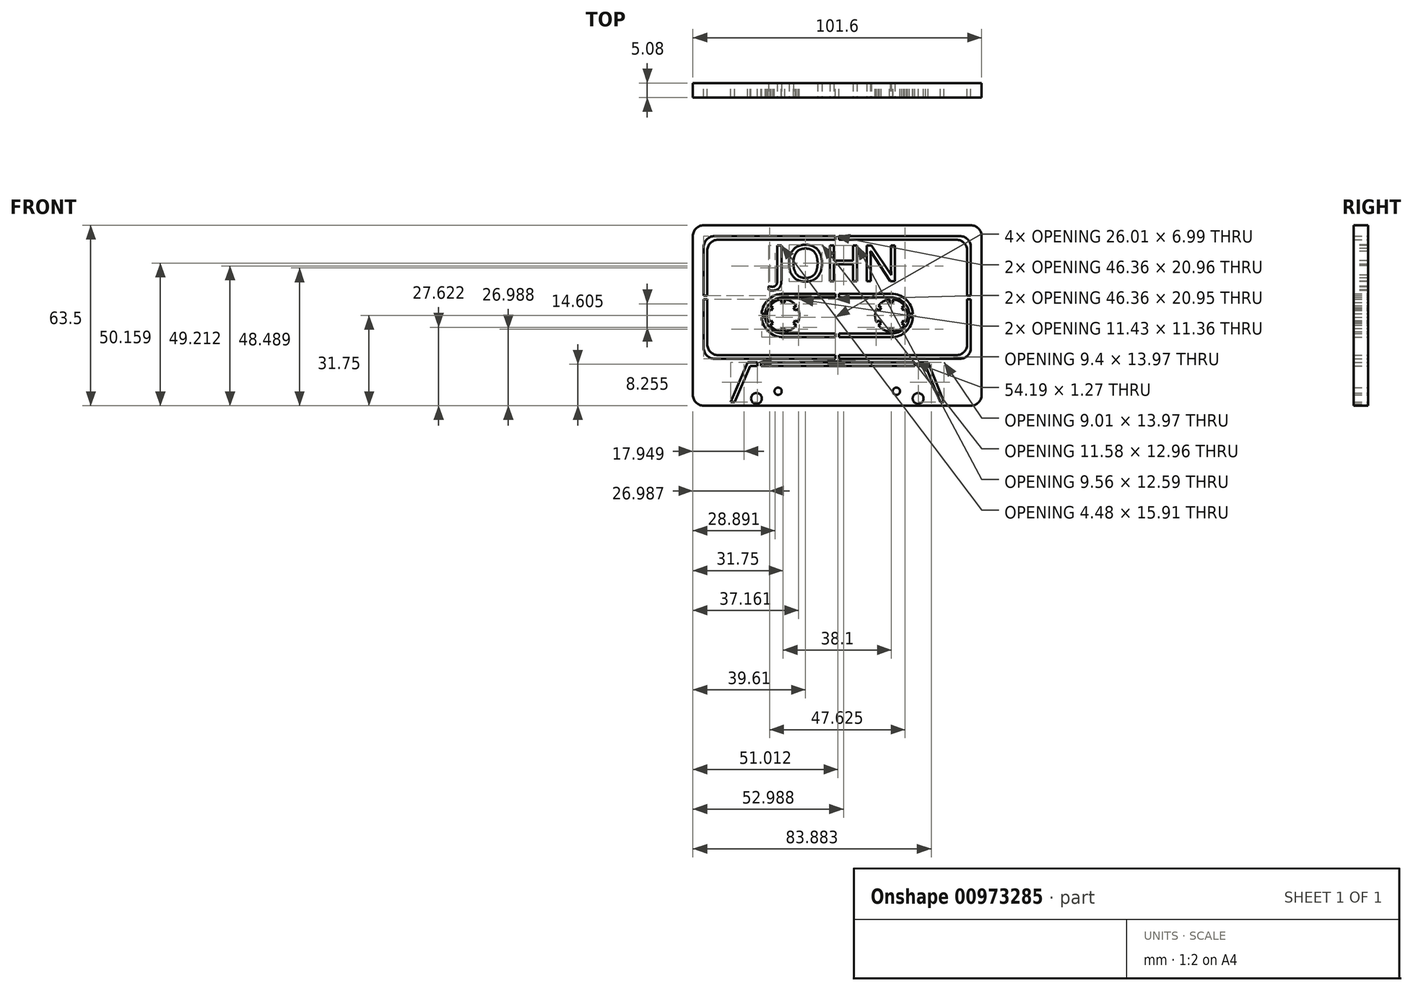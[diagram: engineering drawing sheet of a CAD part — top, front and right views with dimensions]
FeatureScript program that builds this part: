
annotation { "Feature Type Name" : "Feature", "Feature Type Description" : "" }
export const myFeature = defineFeature(function(context is Context, id is Id, definition is map)
    precondition{}
    {
        {
            var Q0;
            Q0=qCreatedBy(makeId("Front.planeOp"),FACE);
            var sketch = newSketch(context, id + "F0", { "sketchPlane" : qUnion([Q0])});
            skLineSegment(sketch, "E0.bottom", {"start": v(47, 31.75) * mm, "end": v(-47, 31.75) * mm});
            skLineSegment(sketch, "E0.top", {"start": v(47, -31.75) * mm, "end": v(-47, -31.75) * mm});
            skLineSegment(sketch, "E0.left", {"start": v(50.8, 27.94) * mm, "end": v(50.8, -27.94) * mm});
            skLineSegment(sketch, "E0.right", {"start": v(-50.8, 27.94) * mm, "end": v(-50.8, -27.94) * mm});
            skPoint(sketch, "E0.middle", {"position": v(0, 0) * mm});
            skPoint(sketch, "E1.visualSharp", {"position": v(50.8, 31.75) * mm});
            skArc(sketch, "E1.filletArc", {"start": v(50.8, 27.94) * mm, "mid": v(49.68, 30.63) * mm, "end": v(47, 31.75) * mm});
            skPoint(sketch, "E2.visualSharp", {"position": v(-50.8, 31.75) * mm});
            skArc(sketch, "E2.filletArc", {"start": v(-47, 31.75) * mm, "mid": v(-49.68, 30.63) * mm, "end": v(-50.8, 27.94) * mm});
            skPoint(sketch, "E3.visualSharp", {"position": v(-50.8, -31.75) * mm});
            skArc(sketch, "E3.filletArc", {"start": v(-50.8, -27.94) * mm, "mid": v(-49.68, -30.63) * mm, "end": v(-47, -31.75) * mm});
            skPoint(sketch, "E4.visualSharp", {"position": v(50.8, -31.75) * mm});
            skArc(sketch, "E4.filletArc", {"start": v(47, -31.75) * mm, "mid": v(49.68, -30.63) * mm, "end": v(50.8, -27.94) * mm});
            skLineSegment(sketch, "E5.bottom", {"start": v(-43.18, 27.94) * mm, "end": v(-0.64, 27.94) * mm});
            skLineSegment(sketch, "E5.top", {"start": v(-43.18, -15.24) * mm, "end": v(-0.64, -15.24) * mm});
            skLineSegment(sketch, "E5.left", {"start": v(-47, 24.13) * mm, "end": v(-47, 6.98) * mm});
            skLineSegment(sketch, "E5.right", {"start": v(47, 24.13) * mm, "end": v(47, 6.99) * mm});
            skLineSegment(sketch, "E6.bottom", {"start": v(-41.91, 26.67) * mm, "end": v(-0.63, 26.67) * mm});
            skLineSegment(sketch, "E6.top", {"start": v(-41.91, -13.97) * mm, "end": v(-0.63, -13.97) * mm});
            skLineSegment(sketch, "E6.left", {"start": v(-45.72, 22.86) * mm, "end": v(-45.72, 6.98) * mm});
            skLineSegment(sketch, "E6.right", {"start": v(45.72, 22.86) * mm, "end": v(45.72, 6.99) * mm});
            skArc(sketch, "E7.filletArc", {"start": v(47, 24.13) * mm, "mid": v(45.87, 26.82) * mm, "end": v(43.18, 27.94) * mm});
            skPoint(sketch, "E8.visualSharp", {"position": v(45.72, 26.67) * mm});
            skArc(sketch, "E8.filletArc", {"start": v(45.72, 22.86) * mm, "mid": v(44.6, 25.55) * mm, "end": v(41.91, 26.67) * mm});
            skPoint(sketch, "E9.visualSharp", {"position": v(47, -15.24) * mm});
            skArc(sketch, "E9.filletArc", {"start": v(43.18, -15.24) * mm, "mid": v(45.87, -14.12) * mm, "end": v(47, -11.43) * mm});
            skPoint(sketch, "E10.visualSharp", {"position": v(45.72, -13.97) * mm});
            skArc(sketch, "E10.filletArc", {"start": v(41.91, -13.97) * mm, "mid": v(44.6, -12.85) * mm, "end": v(45.72, -10.16) * mm});
            skPoint(sketch, "E11.visualSharp", {"position": v(-47, -15.24) * mm});
            skArc(sketch, "E11.filletArc", {"start": v(-47, -11.43) * mm, "mid": v(-45.87, -14.12) * mm, "end": v(-43.18, -15.24) * mm});
            skPoint(sketch, "E12.visualSharp", {"position": v(-45.72, -13.97) * mm});
            skArc(sketch, "E12.filletArc", {"start": v(-45.72, -10.16) * mm, "mid": v(-44.6, -12.85) * mm, "end": v(-41.91, -13.97) * mm});
            skArc(sketch, "E13.filletArc", {"start": v(-43.18, 27.94) * mm, "mid": v(-45.87, 26.82) * mm, "end": v(-47, 24.13) * mm});
            skPoint(sketch, "E14.visualSharp", {"position": v(-45.72, 26.67) * mm});
            skArc(sketch, "E14.filletArc", {"start": v(-41.91, 26.67) * mm, "mid": v(-44.6, 25.55) * mm, "end": v(-45.72, 22.86) * mm});
            skLineSegment(sketch, "E15", {"start": v(0.64, -15.24) * mm, "end": v(0.64, -13.97) * mm});
            skLineSegment(sketch, "E16", {"start": v(-0.64, -15.24) * mm, "end": v(-0.64, -13.97) * mm});
            skLineSegment(sketch, "E17.trimOffspring", {"start": v(-0.64, 26.67) * mm, "end": v(-0.64, 27.94) * mm});
            skLineSegment(sketch, "E18.trimOffspring", {"start": v(0.64, 26.67) * mm, "end": v(0.64, 27.94) * mm});
            skLineSegment(sketch, "E19.trimOffspring", {"start": v(0.63, -13.97) * mm, "end": v(41.91, -13.97) * mm});
            skLineSegment(sketch, "E20.trimOffspring", {"start": v(0.64, -15.24) * mm, "end": v(43.18, -15.24) * mm});
            skLineSegment(sketch, "E21.trimOffspring", {"start": v(0.64, 27.94) * mm, "end": v(43.18, 27.94) * mm});
            skLineSegment(sketch, "E22.trimOffspring", {"start": v(0.63, 26.67) * mm, "end": v(41.91, 26.67) * mm});
            skLineSegment(sketch, "E23", {"start": v(-47, 6.98) * mm, "end": v(-45.72, 6.99) * mm});
            skLineSegment(sketch, "E24", {"start": v(-47, 5.71) * mm, "end": v(-45.72, 5.71) * mm});
            skLineSegment(sketch, "E25.trimOffspring", {"start": v(45.72, 6.99) * mm, "end": v(47, 6.99) * mm});
            skLineSegment(sketch, "E26.trimOffspring", {"start": v(45.72, 5.72) * mm, "end": v(47, 5.72) * mm});
            skPoint(sketch, "E27.orphan", {"position": v(48.52, 5.72) * mm});
            skPoint(sketch, "E28.orphan", {"position": v(48.52, 6.99) * mm});
            skLineSegment(sketch, "E29.trimOffspring", {"start": v(47, 5.72) * mm, "end": v(47, -11.43) * mm});
            skLineSegment(sketch, "E30.trimOffspring", {"start": v(45.72, 5.72) * mm, "end": v(45.72, -10.16) * mm});
            skLineSegment(sketch, "E31.trimOffspring", {"start": v(-45.72, 5.71) * mm, "end": v(-45.72, -10.16) * mm});
            skLineSegment(sketch, "E32.trimOffspring", {"start": v(-47, 5.71) * mm, "end": v(-47, -11.43) * mm});
            skLineSegment(sketch, "E33.bottom", {"start": v(-19.05, 6.35) * mm, "end": v(-0.63, 6.35) * mm});
            skLineSegment(sketch, "E33.top", {"start": v(-19.05, -6.35) * mm, "end": v(-0.63, -6.35) * mm});
            skLineSegment(sketch, "E34.bottom", {"start": v(-19.05, 7.62) * mm, "end": v(-0.63, 7.62) * mm});
            skLineSegment(sketch, "E34.top", {"start": v(-19.05, -7.62) * mm, "end": v(-0.63, -7.62) * mm});
            skLineSegment(sketch, "E35", {"start": v(-0.63, 7.62) * mm, "end": v(-0.63, 6.35) * mm});
            skLineSegment(sketch, "E36", {"start": v(0.63, 7.62) * mm, "end": v(0.63, 6.35) * mm});
            skLineSegment(sketch, "E37.trimOffspring", {"start": v(-0.63, -6.35) * mm, "end": v(-0.63, -7.62) * mm});
            skLineSegment(sketch, "E38.trimOffspring", {"start": v(0.63, -6.35) * mm, "end": v(0.63, -7.62) * mm});
            skLineSegment(sketch, "E39.trimOffspring", {"start": v(0.64, -7.62) * mm, "end": v(19.05, -7.62) * mm});
            skLineSegment(sketch, "E40.trimOffspring", {"start": v(0.63, -6.35) * mm, "end": v(19.05, -6.35) * mm});
            skLineSegment(sketch, "E41.trimOffspring", {"start": v(0.63, 7.62) * mm, "end": v(19.05, 7.62) * mm});
            skLineSegment(sketch, "E42.trimOffspring", {"start": v(0.64, 6.35) * mm, "end": v(23.26, 6.35) * mm});
            skArc(sketch, "E43", {"start": v(-19.69, 5.68) * mm, "mid": v(-21.9, 4.95) * mm, "end": v(-23.65, 3.39) * mm});
            skArc(sketch, "E44", {"start": v(18.41, 5.68) * mm, "mid": v(16.2, 4.95) * mm, "end": v(14.45, 3.39) * mm});
            skArc(sketch, "E45", {"start": v(-19.05, 7.62) * mm, "mid": v(-24.2, 5.6) * mm, "end": v(-26.64, 0.64) * mm});
            skArc(sketch, "E46", {"start": v(-19.05, 6.35) * mm, "mid": v(-23.3, 4.7) * mm, "end": v(-25.37, 0.63) * mm});
            skArc(sketch, "E47", {"start": v(19.05, 7.62) * mm, "mid": v(24.2, 5.6) * mm, "end": v(26.64, 0.64) * mm});
            skArc(sketch, "E48", {"start": v(19.05, 6.35) * mm, "mid": v(23.3, 4.7) * mm, "end": v(25.37, 0.63) * mm});
            skLineSegment(sketch, "E49", {"start": v(-26.64, 0.64) * mm, "end": v(-25.37, 0.64) * mm});
            skLineSegment(sketch, "E50", {"start": v(-26.64, -0.64) * mm, "end": v(-25.37, -0.64) * mm});
            skArc(sketch, "E51.trimOffspring", {"start": v(-26.64, -0.64) * mm, "mid": v(-24.2, -5.6) * mm, "end": v(-19.05, -7.62) * mm});
            skArc(sketch, "E52.trimOffspring", {"start": v(-25.37, -0.64) * mm, "mid": v(-23.3, -4.7) * mm, "end": v(-19.05, -6.35) * mm});
            skLineSegment(sketch, "E53.trimOffspring", {"start": v(25.37, 0.64) * mm, "end": v(26.64, 0.64) * mm});
            skLineSegment(sketch, "E54.trimOffspring", {"start": v(25.37, -0.64) * mm, "end": v(26.64, -0.64) * mm});
            skArc(sketch, "E55.trimOffspring", {"start": v(25.37, -0.64) * mm, "mid": v(23.3, -4.7) * mm, "end": v(19.05, -6.35) * mm});
            skArc(sketch, "E56.trimOffspring", {"start": v(26.64, -0.64) * mm, "mid": v(24.2, -5.6) * mm, "end": v(19.05, -7.62) * mm});
            skLineSegment(sketch, "E57", {"start": v(-18.41, 5.68) * mm, "end": v(-18.41, 4.57) * mm});
            skLineSegment(sketch, "E58", {"start": v(-18.41, 4.57) * mm, "end": v(-19.69, 4.57) * mm});
            skLineSegment(sketch, "E59", {"start": v(-19.69, 4.57) * mm, "end": v(-19.69, 5.68) * mm});
            skLineSegment(sketch, "E60.MirrorCS", {"start": v(18.41, 5.68) * mm, "end": v(18.41, 4.57) * mm});
            skLineSegment(sketch, "E61.MirrorCS", {"start": v(18.41, 4.57) * mm, "end": v(19.69, 4.57) * mm});
            skLineSegment(sketch, "E62.MirrorCS", {"start": v(19.69, 4.57) * mm, "end": v(19.69, 5.68) * mm});
            skLineSegment(sketch, "E63.1.0", {"start": v(-23.65, 3.39) * mm, "end": v(-22.7, 2.84) * mm});
            skLineSegment(sketch, "E63.1.1", {"start": v(-22.7, 2.84) * mm, "end": v(-23.33, 1.74) * mm});
            skLineSegment(sketch, "E63.1.2", {"start": v(-23.33, 1.74) * mm, "end": v(-24.29, 2.29) * mm});
            skLineSegment(sketch, "E63.2.0", {"start": v(-24.29, -2.29) * mm, "end": v(-23.33, -1.74) * mm});
            skLineSegment(sketch, "E63.2.1", {"start": v(-23.33, -1.74) * mm, "end": v(-22.7, -2.84) * mm});
            skLineSegment(sketch, "E63.2.2", {"start": v(-22.7, -2.84) * mm, "end": v(-23.65, -3.39) * mm});
            skLineSegment(sketch, "E63.3.0", {"start": v(-19.69, -5.68) * mm, "end": v(-19.69, -4.57) * mm});
            skLineSegment(sketch, "E63.3.1", {"start": v(-19.69, -4.57) * mm, "end": v(-18.41, -4.57) * mm});
            skLineSegment(sketch, "E63.3.2", {"start": v(-18.41, -4.57) * mm, "end": v(-18.41, -5.68) * mm});
            skLineSegment(sketch, "E63.4.0", {"start": v(-14.45, -3.39) * mm, "end": v(-15.4, -2.84) * mm});
            skLineSegment(sketch, "E63.4.1", {"start": v(-15.4, -2.84) * mm, "end": v(-14.77, -1.74) * mm});
            skLineSegment(sketch, "E63.4.2", {"start": v(-14.77, -1.74) * mm, "end": v(-13.81, -2.29) * mm});
            skLineSegment(sketch, "E63.5.0", {"start": v(-13.81, 2.29) * mm, "end": v(-14.77, 1.74) * mm});
            skLineSegment(sketch, "E63.5.1", {"start": v(-14.77, 1.74) * mm, "end": v(-15.4, 2.84) * mm});
            skLineSegment(sketch, "E63.5.2", {"start": v(-15.4, 2.84) * mm, "end": v(-14.45, 3.39) * mm});
            skArc(sketch, "E64.trimOffspring", {"start": v(-14.45, 3.39) * mm, "mid": v(-16.2, 4.95) * mm, "end": v(-18.41, 5.68) * mm});
            skArc(sketch, "E65.trimOffspring", {"start": v(-13.81, -2.29) * mm, "mid": v(-13.33, 0) * mm, "end": v(-13.81, 2.29) * mm});
            skArc(sketch, "E66.trimOffspring", {"start": v(-18.41, -5.68) * mm, "mid": v(-16.2, -4.95) * mm, "end": v(-14.45, -3.39) * mm});
            skArc(sketch, "E67.trimOffspring", {"start": v(-23.65, -3.39) * mm, "mid": v(-21.9, -4.95) * mm, "end": v(-19.69, -5.68) * mm});
            skArc(sketch, "E68.trimOffspring", {"start": v(-24.29, 2.29) * mm, "mid": v(-24.77, 0) * mm, "end": v(-24.29, -2.29) * mm});
            skLineSegment(sketch, "E69.1.0", {"start": v(15.4, 2.84) * mm, "end": v(14.45, 3.39) * mm});
            skLineSegment(sketch, "E69.1.1", {"start": v(14.77, 1.74) * mm, "end": v(15.4, 2.84) * mm});
            skLineSegment(sketch, "E69.1.2", {"start": v(13.81, 2.29) * mm, "end": v(14.77, 1.74) * mm});
            skLineSegment(sketch, "E69.2.0", {"start": v(14.77, -1.74) * mm, "end": v(13.81, -2.29) * mm});
            skLineSegment(sketch, "E69.2.1", {"start": v(15.4, -2.84) * mm, "end": v(14.77, -1.74) * mm});
            skLineSegment(sketch, "E69.2.2", {"start": v(14.45, -3.39) * mm, "end": v(15.4, -2.84) * mm});
            skLineSegment(sketch, "E69.3.0", {"start": v(18.41, -4.57) * mm, "end": v(18.41, -5.68) * mm});
            skLineSegment(sketch, "E69.3.1", {"start": v(19.69, -4.57) * mm, "end": v(18.41, -4.57) * mm});
            skLineSegment(sketch, "E69.3.2", {"start": v(19.69, -5.68) * mm, "end": v(19.69, -4.57) * mm});
            skLineSegment(sketch, "E69.4.0", {"start": v(22.7, -2.84) * mm, "end": v(23.65, -3.39) * mm});
            skLineSegment(sketch, "E69.4.1", {"start": v(23.33, -1.74) * mm, "end": v(22.7, -2.84) * mm});
            skLineSegment(sketch, "E69.4.2", {"start": v(24.29, -2.29) * mm, "end": v(23.33, -1.74) * mm});
            skLineSegment(sketch, "E69.5.0", {"start": v(23.33, 1.74) * mm, "end": v(24.29, 2.29) * mm});
            skLineSegment(sketch, "E69.5.1", {"start": v(22.7, 2.84) * mm, "end": v(23.33, 1.74) * mm});
            skLineSegment(sketch, "E69.5.2", {"start": v(23.65, 3.39) * mm, "end": v(22.7, 2.84) * mm});
            skArc(sketch, "E70.trimOffspring", {"start": v(23.65, 3.39) * mm, "mid": v(21.9, 4.95) * mm, "end": v(19.69, 5.68) * mm});
            skArc(sketch, "E71.trimOffspring", {"start": v(24.29, -2.29) * mm, "mid": v(24.77, 0) * mm, "end": v(24.29, 2.29) * mm});
            skArc(sketch, "E72.trimOffspring", {"start": v(19.69, -5.68) * mm, "mid": v(21.9, -4.95) * mm, "end": v(23.65, -3.39) * mm});
            skArc(sketch, "E73.trimOffspring", {"start": v(14.45, -3.39) * mm, "mid": v(16.2, -4.95) * mm, "end": v(18.41, -5.68) * mm});
            skArc(sketch, "E74.trimOffspring", {"start": v(13.81, 2.29) * mm, "mid": v(13.33, 0) * mm, "end": v(13.81, -2.29) * mm});
            skLineSegment(sketch, "E75", {"start": v(-37.55, -30.48) * mm, "end": v(-31.53, -16.51) * mm});
            skLineSegment(sketch, "E76", {"start": v(-31.53, -16.51) * mm, "end": v(-28.15, -16.51) * mm});
            skLineSegment(sketch, "E77", {"start": v(31.97, -16.5) * mm, "end": v(37.59, -30.48) * mm});
            skLineSegment(sketch, "E78", {"start": v(-36.17, -30.48) * mm, "end": v(-30.7, -17.78) * mm});
            skLineSegment(sketch, "E79", {"start": v(-30.7, -17.78) * mm, "end": v(-28.15, -17.78) * mm});
            skLineSegment(sketch, "E80", {"start": v(31.12, -17.78) * mm, "end": v(36.22, -30.48) * mm});
            skLineSegment(sketch, "E81", {"start": v(-37.55, -30.48) * mm, "end": v(-36.17, -30.48) * mm});
            skLineSegment(sketch, "E82.trimOffspring", {"start": v(36.22, -30.48) * mm, "end": v(37.59, -30.48) * mm});
            skPoint(sketch, "E83.orphan", {"position": v(-38.1, -31.75) * mm});
            skPoint(sketch, "E84.orphan", {"position": v(38.1, -31.75) * mm});
            skLineSegment(sketch, "E85", {"start": v(-28.15, -17.78) * mm, "end": v(-28.15, -16.51) * mm});
            skLineSegment(sketch, "E86", {"start": v(-26.88, -16.51) * mm, "end": v(-26.88, -17.78) * mm});
            skLineSegment(sketch, "E87.trimOffspring", {"start": v(-26.88, -16.51) * mm, "end": v(27.3, -16.5) * mm});
            skLineSegment(sketch, "E88.trimOffspring", {"start": v(-26.88, -17.78) * mm, "end": v(27.3, -17.78) * mm});
            skLineSegment(sketch, "E89.MirrorCS", {"start": v(27.3, -16.5) * mm, "end": v(27.3, -17.78) * mm});
            skLineSegment(sketch, "E90.MirrorCS", {"start": v(28.58, -17.78) * mm, "end": v(28.58, -16.5) * mm});
            skLineSegment(sketch, "E91.trimOffspring", {"start": v(28.58, -16.5) * mm, "end": v(31.97, -16.5) * mm});
            skLineSegment(sketch, "E92.trimOffspring", {"start": v(28.58, -17.78) * mm, "end": v(31.12, -17.78) * mm});
            skCircle(sketch, "E93", {"center": v(-28.44, -29.21) * mm, "radius": 1.9 * mm});
            skCircle(sketch, "E94", {"center": v(-20.82, -26.67) * mm, "radius": 1.27 * mm});
            skCircle(sketch, "E95.MirrorC", {"center": v(20.82, -26.67) * mm, "radius": 1.27 * mm});
            skCircle(sketch, "E96.MirrorC", {"center": v(28.44, -29.21) * mm, "radius": 1.9 * mm});
            skSolve(sketch);
        }
        {
            var Q0;
            Q0=qSketchRegion(id+"F0",true);
            extrude(context, id + "F1", {"entities" : qUnion([Q0]), "depth" : 5.08 * mm, "offsetDistance" : 25.4 * mm});
        }
        {
            var Q0;
            Q0=makeQuery(id+"F1.opExtrude","CAP_FACE",FACE,{"disambiguationData":[OSD([sQuery(id+"F0.wireOp",EDGE,"E0.bottom"),sQuery(id+"F0.wireOp",EDGE,"E0.top"),sQuery(id+"F0.wireOp",EDGE,"E0.left"),sQuery(id+"F0.wireOp",EDGE,"E0.right"),sQuery(id+"F0.wireOp",EDGE,"E1.filletArc"),sQuery(id+"F0.wireOp",EDGE,"E2.filletArc"),sQuery(id+"F0.wireOp",EDGE,"E3.filletArc"),sQuery(id+"F0.wireOp",EDGE,"E4.filletArc"),sQuery(id+"F0.wireOp",EDGE,"E5.bottom"),sQuery(id+"F0.wireOp",EDGE,"E5.top"),sQuery(id+"F0.wireOp",EDGE,"E5.left"),sQuery(id+"F0.wireOp",EDGE,"E5.right"),sQuery(id+"F0.wireOp",EDGE,"E6.bottom"),sQuery(id+"F0.wireOp",EDGE,"E6.top"),sQuery(id+"F0.wireOp",EDGE,"E6.left"),sQuery(id+"F0.wireOp",EDGE,"E6.right"),sQuery(id+"F0.wireOp",EDGE,"E7.filletArc"),sQuery(id+"F0.wireOp",EDGE,"E8.filletArc"),sQuery(id+"F0.wireOp",EDGE,"E9.filletArc"),sQuery(id+"F0.wireOp",EDGE,"E10.filletArc"),sQuery(id+"F0.wireOp",EDGE,"E11.filletArc"),sQuery(id+"F0.wireOp",EDGE,"E12.filletArc"),sQuery(id+"F0.wireOp",EDGE,"E13.filletArc"),sQuery(id+"F0.wireOp",EDGE,"E14.filletArc"),sQuery(id+"F0.wireOp",EDGE,"E15"),sQuery(id+"F0.wireOp",EDGE,"E16"),sQuery(id+"F0.wireOp",EDGE,"E17.trimOffspring"),sQuery(id+"F0.wireOp",EDGE,"E18.trimOffspring"),sQuery(id+"F0.wireOp",EDGE,"E19.trimOffspring"),sQuery(id+"F0.wireOp",EDGE,"E20.trimOffspring"),sQuery(id+"F0.wireOp",EDGE,"E21.trimOffspring"),sQuery(id+"F0.wireOp",EDGE,"E22.trimOffspring"),sQuery(id+"F0.wireOp",EDGE,"E23"),sQuery(id+"F0.wireOp",EDGE,"E24"),sQuery(id+"F0.wireOp",EDGE,"E25.trimOffspring"),sQuery(id+"F0.wireOp",EDGE,"E26.trimOffspring"),sQuery(id+"F0.wireOp",EDGE,"E29.trimOffspring"),sQuery(id+"F0.wireOp",EDGE,"E30.trimOffspring"),sQuery(id+"F0.wireOp",EDGE,"E31.trimOffspring"),sQuery(id+"F0.wireOp",EDGE,"E32.trimOffspring"),sQuery(id+"F0.wireOp",EDGE,"E33.bottom"),sQuery(id+"F0.wireOp",EDGE,"E33.top"),sQuery(id+"F0.wireOp",EDGE,"E34.bottom"),sQuery(id+"F0.wireOp",EDGE,"E34.top"),sQuery(id+"F0.wireOp",EDGE,"E35"),sQuery(id+"F0.wireOp",EDGE,"E36"),sQuery(id+"F0.wireOp",EDGE,"E37.trimOffspring"),sQuery(id+"F0.wireOp",EDGE,"E38.trimOffspring"),sQuery(id+"F0.wireOp",EDGE,"E39.trimOffspring"),sQuery(id+"F0.wireOp",EDGE,"E40.trimOffspring"),sQuery(id+"F0.wireOp",EDGE,"E41.trimOffspring"),sQuery(id+"F0.wireOp",EDGE,"E42.trimOffspring"),sQuery(id+"F0.wireOp",EDGE,"E43"),sQuery(id+"F0.wireOp",EDGE,"E44"),sQuery(id+"F0.wireOp",EDGE,"E45"),sQuery(id+"F0.wireOp",EDGE,"E46"),sQuery(id+"F0.wireOp",EDGE,"E47"),sQuery(id+"F0.wireOp",EDGE,"E48"),sQuery(id+"F0.wireOp",EDGE,"E49"),sQuery(id+"F0.wireOp",EDGE,"E50"),sQuery(id+"F0.wireOp",EDGE,"E51.trimOffspring"),sQuery(id+"F0.wireOp",EDGE,"E52.trimOffspring"),sQuery(id+"F0.wireOp",EDGE,"E53.trimOffspring"),sQuery(id+"F0.wireOp",EDGE,"E54.trimOffspring"),sQuery(id+"F0.wireOp",EDGE,"E55.trimOffspring"),sQuery(id+"F0.wireOp",EDGE,"E56.trimOffspring"),sQuery(id+"F0.wireOp",EDGE,"E57"),sQuery(id+"F0.wireOp",EDGE,"E58"),sQuery(id+"F0.wireOp",EDGE,"E59"),sQuery(id+"F0.wireOp",EDGE,"E60.MirrorCS"),sQuery(id+"F0.wireOp",EDGE,"E61.MirrorCS"),sQuery(id+"F0.wireOp",EDGE,"E62.MirrorCS"),sQuery(id+"F0.wireOp",EDGE,"E63.1.0"),sQuery(id+"F0.wireOp",EDGE,"E63.1.1"),sQuery(id+"F0.wireOp",EDGE,"E63.1.2"),sQuery(id+"F0.wireOp",EDGE,"E63.2.0"),sQuery(id+"F0.wireOp",EDGE,"E63.2.1"),sQuery(id+"F0.wireOp",EDGE,"E63.2.2"),sQuery(id+"F0.wireOp",EDGE,"E63.3.0"),sQuery(id+"F0.wireOp",EDGE,"E63.3.1"),sQuery(id+"F0.wireOp",EDGE,"E63.3.2"),sQuery(id+"F0.wireOp",EDGE,"E63.4.0"),sQuery(id+"F0.wireOp",EDGE,"E63.4.1"),sQuery(id+"F0.wireOp",EDGE,"E63.4.2"),sQuery(id+"F0.wireOp",EDGE,"E63.5.0"),sQuery(id+"F0.wireOp",EDGE,"E63.5.1"),sQuery(id+"F0.wireOp",EDGE,"E63.5.2"),sQuery(id+"F0.wireOp",EDGE,"E64.trimOffspring"),sQuery(id+"F0.wireOp",EDGE,"E65.trimOffspring"),sQuery(id+"F0.wireOp",EDGE,"E66.trimOffspring"),sQuery(id+"F0.wireOp",EDGE,"E67.trimOffspring"),sQuery(id+"F0.wireOp",EDGE,"E68.trimOffspring"),sQuery(id+"F0.wireOp",EDGE,"E69.1.0"),sQuery(id+"F0.wireOp",EDGE,"E69.1.1"),sQuery(id+"F0.wireOp",EDGE,"E69.1.2"),sQuery(id+"F0.wireOp",EDGE,"E69.2.0"),sQuery(id+"F0.wireOp",EDGE,"E69.2.1"),sQuery(id+"F0.wireOp",EDGE,"E69.2.2"),sQuery(id+"F0.wireOp",EDGE,"E69.3.0"),sQuery(id+"F0.wireOp",EDGE,"E69.3.1"),sQuery(id+"F0.wireOp",EDGE,"E69.3.2"),sQuery(id+"F0.wireOp",EDGE,"E69.4.0"),sQuery(id+"F0.wireOp",EDGE,"E69.4.1"),sQuery(id+"F0.wireOp",EDGE,"E69.4.2"),sQuery(id+"F0.wireOp",EDGE,"E69.5.0"),sQuery(id+"F0.wireOp",EDGE,"E69.5.1"),sQuery(id+"F0.wireOp",EDGE,"E69.5.2"),sQuery(id+"F0.wireOp",EDGE,"E70.trimOffspring"),sQuery(id+"F0.wireOp",EDGE,"E71.trimOffspring"),sQuery(id+"F0.wireOp",EDGE,"E72.trimOffspring"),sQuery(id+"F0.wireOp",EDGE,"E73.trimOffspring"),sQuery(id+"F0.wireOp",EDGE,"E74.trimOffspring"),sQuery(id+"F0.wireOp",EDGE,"E75"),sQuery(id+"F0.wireOp",EDGE,"E76"),sQuery(id+"F0.wireOp",EDGE,"E77"),sQuery(id+"F0.wireOp",EDGE,"E78"),sQuery(id+"F0.wireOp",EDGE,"E79"),sQuery(id+"F0.wireOp",EDGE,"E80"),sQuery(id+"F0.wireOp",EDGE,"E81"),sQuery(id+"F0.wireOp",EDGE,"E82.trimOffspring"),sQuery(id+"F0.wireOp",EDGE,"E85"),sQuery(id+"F0.wireOp",EDGE,"E86"),sQuery(id+"F0.wireOp",EDGE,"E87.trimOffspring"),sQuery(id+"F0.wireOp",EDGE,"E88.trimOffspring"),sQuery(id+"F0.wireOp",EDGE,"E89.MirrorCS"),sQuery(id+"F0.wireOp",EDGE,"E90.MirrorCS"),sQuery(id+"F0.wireOp",EDGE,"E91.trimOffspring"),sQuery(id+"F0.wireOp",EDGE,"E92.trimOffspring"),sQuery(id+"F0.wireOp",EDGE,"E93"),sQuery(id+"F0.wireOp",EDGE,"E94"),sQuery(id+"F0.wireOp",EDGE,"E95.MirrorC"),sQuery(id+"F0.wireOp",EDGE,"E96.MirrorC")])],"isStart":false});
            var sketch = newSketch(context, id + "F2", { "sketchPlane" : qUnion([Q0])});
            skText(sketch, "E97", { "text": "JOHN\n", "fontName": "OpenSans-Regular.ttf"});
            const initialGuessF2  = {"E97": [-0.02277, 0.0121, 1, 0, 0.0127]};
            skSetInitialGuess(sketch, initialGuessF2);
            skSolve(sketch);
        }
        {
            var Q0;
            Q0=qSketchRegion(id+"F2",true);
            extrude(context, id + "F3", {"entities" : qUnion([Q0]), "operationType" : NewBodyOperationType.REMOVE, "oppositeDirection" : true, "depth" : 25.4 * mm, "offsetDistance" : 25.4 * mm});
        }
    });
